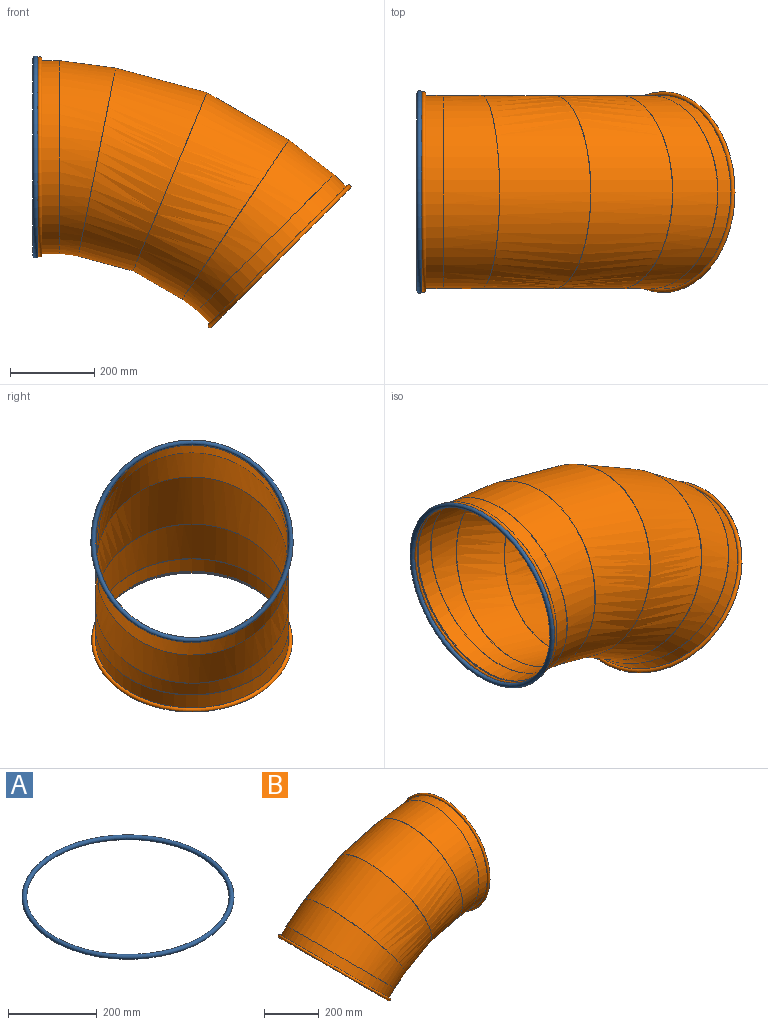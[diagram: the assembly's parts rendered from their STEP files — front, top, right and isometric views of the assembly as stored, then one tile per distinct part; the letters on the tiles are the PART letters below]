
ASSEMBLY  parts=2 mates=1
PART A: 1 faces, bbox 518.7x518.7x11 mm
  f0: torus R=234.1mm, axis (0,0,-1), area 50830.4mm2
PART B: 18 faces, bbox 755.6x914.4x675.6 mm
  f0: cylinder r=228.6mm len=457.2mm, axis (-1,0,0), area 65669.3mm2, adj f4,f6
  f1: cylinder r=227.58mm len=455.17mm, axis (-1,0,0), area 65377.4mm2, adj f2,f8
  f2: torus R=232.66mm, axis (-1,0,0), area 41400.9mm2, adj f1,f3
  f3: cylinder r=228.85mm len=457.71mm, axis (-1,0,0), area 2798.1mm2, adj f2,f4
  f4: torus R=232.66mm, axis (-1,0,0), area 35253.2mm2, adj f0,f3
  f5: bspline ~914.4x520.93mm, area 256660.8mm2, adj f6,f14
  f6: bspline ~914.4x475.42mm, area 129470.7mm2, adj f0,f5
  f7: bspline ~910.34x518.82mm, area 255519.6mm2, adj f8,f16
  f8: bspline ~910.34x473.35mm, area 128894.8mm2, adj f1,f7
  f9: cylinder r=228.6mm len=457.2mm, axis (0.71,0,0.71), area 65669.3mm2, adj f13,f15
  f10: cylinder r=227.58mm len=455.17mm, axis (0.71,0,0.71), area 65377.4mm2, adj f11,f17
  f11: torus R=232.66mm, axis (0.71,0,0.71), area 41400.9mm2, adj f10,f12
  f12: cylinder r=228.85mm len=457.71mm, axis (0.71,0,0.71), area 2798.1mm2, adj f11,f13
  f13: torus R=232.66mm, axis (0.71,0,0.71), area 35253.2mm2, adj f9,f12
  f14: bspline ~914.4x504.67mm, area 256660.8mm2, adj f5,f15
  f15: bspline ~914.4x434mm, area 129470.7mm2, adj f9,f14
  f16: bspline ~910.34x503.11mm, area 255519.6mm2, adj f7,f17
  f17: bspline ~910.34x432.39mm, area 128894.8mm2, adj f10,f16
PLACE A rot(axis=(0,1,0),90deg) t=(-2177.35,990.63,9169.4)mm
PLACE B rot(axis=(0,0,1),180deg) t=(-2121.05,990.63,8477.68)mm
MATE fastened A.f0 <-> B.f0  axis (1,0,0) through (-2171.85,990.63,9169.4)mm
